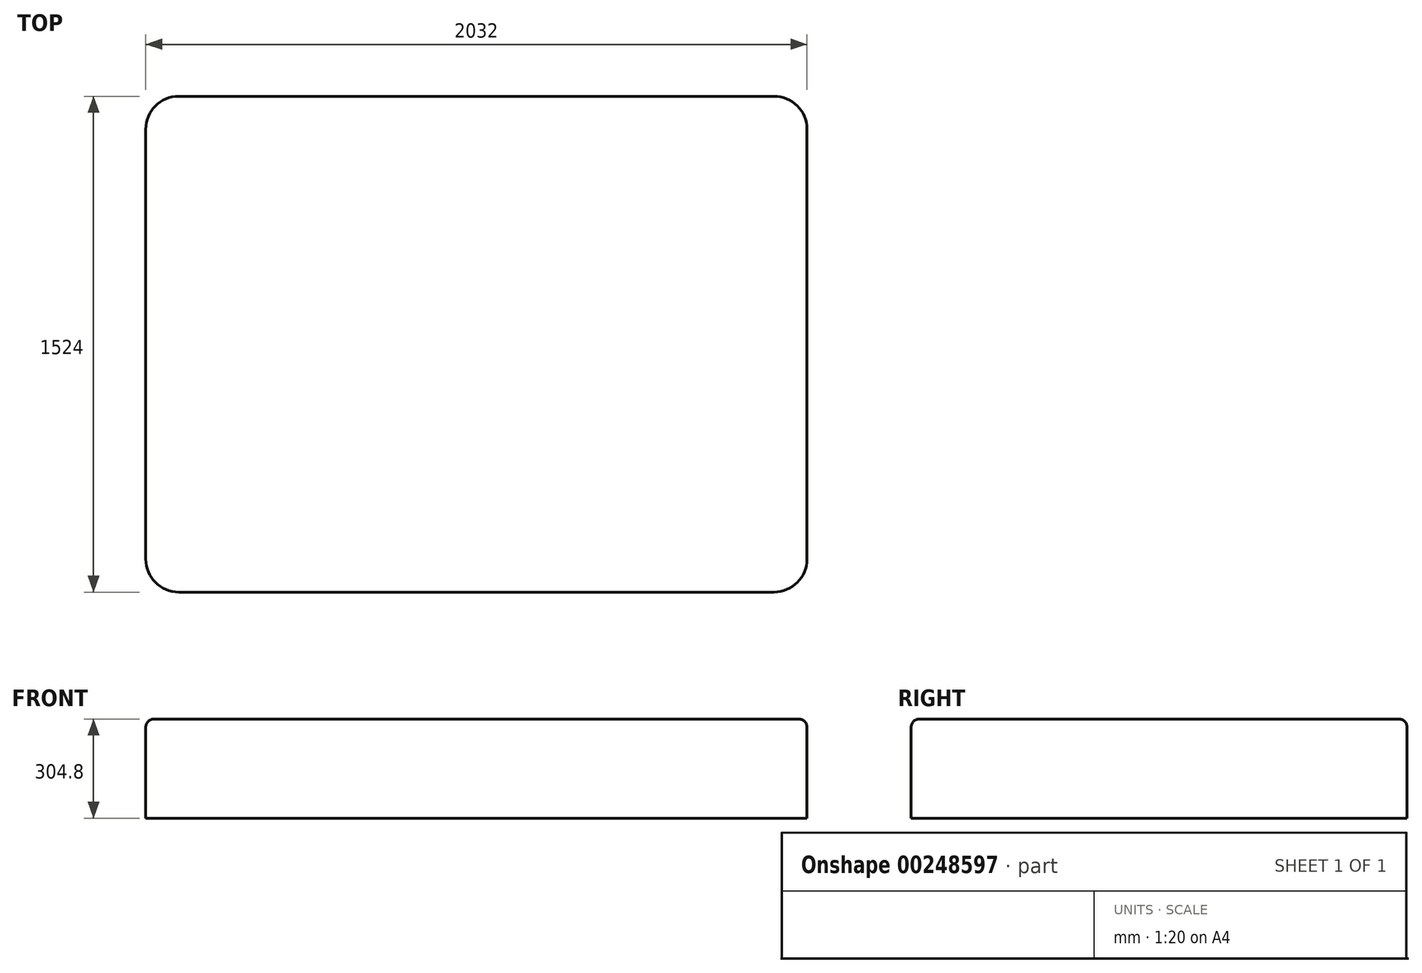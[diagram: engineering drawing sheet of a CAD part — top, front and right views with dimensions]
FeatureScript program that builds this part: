
annotation { "Feature Type Name" : "Feature", "Feature Type Description" : "" }
export const myFeature = defineFeature(function(context is Context, id is Id, definition is map)
    precondition{}
    {
        {
            var Q0;
            Q0=qCreatedBy(makeId("Top.planeOp"),FACE);
            var sketch = newSketch(context, id + "F0", { "sketchPlane" : qUnion([Q0])});
            skLineSegment(sketch, "E0.bottom", {"start": v(-1011.68, 1029.63) * mm, "end": v(1020.32, 1029.63) * mm});
            skLineSegment(sketch, "E0.top", {"start": v(-1011.68, -494.37) * mm, "end": v(1020.32, -494.37) * mm});
            skLineSegment(sketch, "E0.left", {"start": v(-1011.68, 1029.63) * mm, "end": v(-1011.68, -494.37) * mm});
            skLineSegment(sketch, "E0.right", {"start": v(1020.32, 1029.63) * mm, "end": v(1020.32, -494.37) * mm});
            skSolve(sketch);
        }
        {
            var Q0;
            Q0=makeQuery(id+"F0.imprint","IMPRINT",FACE,{"disambiguationData":[TD([[makeQuery(id+"F0.imprint","IMPRINT",EDGE,{"derivedFrom":sQuery(id+"F0.wireOp",EDGE,"E0.bottom")}),-1.0]])]});
            extrude(context, id + "F1", {"entities" : qUnion([Q0]), "depth" : 304.8 * mm});
        }
        {
            var Q0;
            Q0=makeQuery(id+"F1.opExtrude","SWEPT_EDGE",EDGE,{"disambiguationData":[OSD([sQuery(id+"F0.wireOp",EDGE,"E0.top"),sQuery(id+"F0.wireOp",EDGE,"E0.left")])]});
            fillet(context, id + "F2", {"entities" : qUnion([Q0]), "radius" : 101.6 * mm, "tangentPropagation" : true, "allowEdgeOverflow" : false});
        }
        {
            var Q0;
            Q0=makeQuery(id+"F1.opExtrude","SWEPT_EDGE",EDGE,{"disambiguationData":[OSD([sQuery(id+"F0.wireOp",EDGE,"E0.bottom"),sQuery(id+"F0.wireOp",EDGE,"E0.left")])]});
            fillet(context, id + "F3", {"entities" : qUnion([Q0]), "radius" : 101.6 * mm, "tangentPropagation" : true, "allowEdgeOverflow" : false});
        }
        {
            var Q0;
            Q0=makeQuery(id+"F1.opExtrude","SWEPT_EDGE",EDGE,{"disambiguationData":[OSD([sQuery(id+"F0.wireOp",EDGE,"E0.bottom"),sQuery(id+"F0.wireOp",EDGE,"E0.right")])]});
            fillet(context, id + "F4", {"entities" : qUnion([Q0]), "radius" : 101.6 * mm, "tangentPropagation" : true, "allowEdgeOverflow" : false});
        }
        {
            var Q0;
            Q0=makeQuery(id+"F1.opExtrude","SWEPT_EDGE",EDGE,{"disambiguationData":[OSD([sQuery(id+"F0.wireOp",EDGE,"E0.top"),sQuery(id+"F0.wireOp",EDGE,"E0.right")])]});
            fillet(context, id + "F5", {"entities" : qUnion([Q0]), "radius" : 101.6 * mm, "tangentPropagation" : true, "allowEdgeOverflow" : false});
        }
        {
            var Q0;
            Q0=makeQuery(id+"F1.opExtrude","CAP_EDGE",EDGE,{"disambiguationData":[OSD([sQuery(id+"F0.wireOp",EDGE,"E0.left")])],"isStart":false});
            var Q1;
            Q1=makeQuery(id+"F1.opExtrude","CAP_EDGE",EDGE,{"disambiguationData":[OSD([sQuery(id+"F0.wireOp",EDGE,"E0.bottom")])],"isStart":false});
            var Q2;
            Q2=makeQuery(id+"F1.opExtrude","CAP_EDGE",EDGE,{"disambiguationData":[OSD([sQuery(id+"F0.wireOp",EDGE,"E0.top")])],"isStart":false});
            var Q3;
            Q3=makeQuery(id+"F1.opExtrude","CAP_EDGE",EDGE,{"disambiguationData":[OSD([sQuery(id+"F0.wireOp",EDGE,"E0.right")])],"isStart":false});
            fillet(context, id + "F6", {"entities" : qUnion([Q0, Q1, Q2, Q3]), "radius" : 25.4 * mm, "tangentPropagation" : true, "allowEdgeOverflow" : false});
        }
    });
